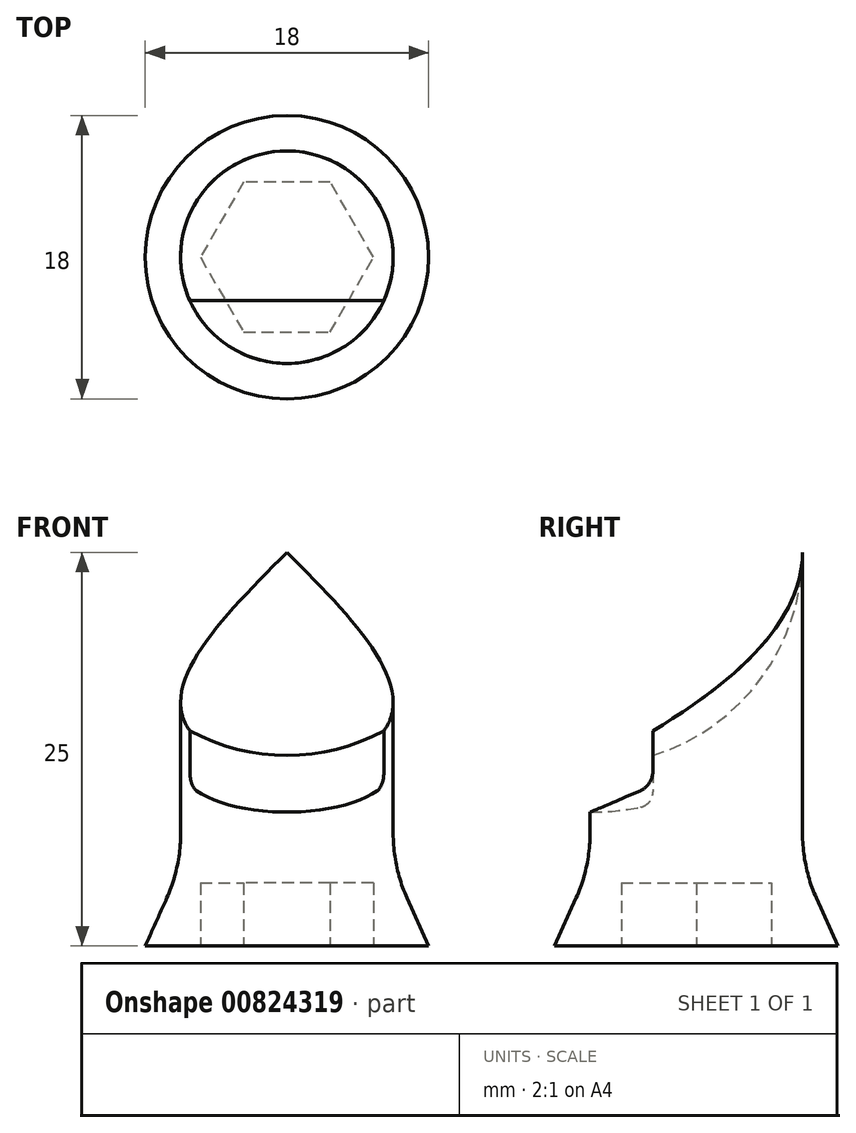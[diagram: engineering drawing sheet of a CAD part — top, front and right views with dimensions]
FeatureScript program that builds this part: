
annotation { "Feature Type Name" : "Feature", "Feature Type Description" : "" }
export const myFeature = defineFeature(function(context is Context, id is Id, definition is map)
    precondition{}
    {
        {
            var Q0;
            Q0=qCreatedBy(makeId("Right.planeOp"),FACE);
            var sketch = newSketch(context, id + "F0", { "sketchPlane" : qUnion([Q0])});
            skArc(sketch, "E0", {"start": v(11.5, 0) * mm, "mid": v(8.13, 8.13) * mm, "end": v(0, 11.5) * mm});
            skArc(sketch, "E1.0", {"start": v(13.5, 0) * mm, "mid": v(9.55, 9.55) * mm, "end": v(0, 13.5) * mm});
            skLineSegment(sketch, "E2", {"start": v(0, 13.5) * mm, "end": v(0, 11.5) * mm});
            skLineSegment(sketch, "E3.0", {"start": v(3, 15.75) * mm, "end": v(3, 13.75) * mm});
            skLineSegment(sketch, "E4.0", {"start": v(4, 15.2) * mm, "end": v(4, 12.9) * mm});
            skArc(sketch, "E5.0", {"start": v(3.2, 16.19) * mm, "mid": v(1.6, 16.42) * mm, "end": v(0, 16.5) * mm});
            skLineSegment(sketch, "E6", {"start": v(0, 16.5) * mm, "end": v(0, 16) * mm});
            skLineSegment(sketch, "E7.trimOffspring", {"start": v(2.75, 16) * mm, "end": v(0, 16) * mm});
            skArc(sketch, "E8.filletArc", {"start": v(4, 15.2) * mm, "mid": v(3.77, 15.84) * mm, "end": v(3.2, 16.19) * mm});
            skPoint(sketch, "E9.visualSharp", {"position": v(3, 16) * mm});
            skArc(sketch, "E9.filletArc", {"start": v(3, 15.75) * mm, "mid": v(2.93, 15.93) * mm, "end": v(2.75, 16) * mm});
            skLineSegment(sketch, "E10.0", {"start": v(2.75, 13.5) * mm, "end": v(0, 13.5) * mm});
            skPoint(sketch, "E11.visualSharp", {"position": v(3, 13.5) * mm});
            skArc(sketch, "E11.filletArc", {"start": v(2.75, 13.5) * mm, "mid": v(2.93, 13.57) * mm, "end": v(3, 13.75) * mm});
            skLineSegment(sketch, "E12", {"start": v(11.5, 0) * mm, "end": v(13.5, 0) * mm});
            skLineSegment(sketch, "E13", {"start": v(0, 0) * mm, "end": v(-5, 0) * mm, "construction": true});
            skPoint(sketch, "E14.orphan", {"position": v(13.5, 0) * mm});
            skLineSegment(sketch, "E15.bottom", {"start": v(6.75, 0) * mm, "end": v(13.5, 0) * mm});
            skLineSegment(sketch, "E15.right", {"start": v(13.5, 0) * mm, "end": v(13.5, -17.85) * mm});
            skLineSegment(sketch, "E16.0", {"start": v(6.75, -25) * mm, "end": v(15.75, -25) * mm});
            skLineSegment(sketch, "E17", {"start": v(6.75, -25) * mm, "end": v(6.75, 0) * mm});
            skLineSegment(sketch, "E18", {"start": v(14.38, -21.96) * mm, "end": v(15.75, -25) * mm});
            skPoint(sketch, "E19.visualSharp", {"position": v(0, -21.07) * mm});
            skPoint(sketch, "E20.visualSharp", {"position": v(13.5, -20) * mm});
            skArc(sketch, "E20.filletArc", {"start": v(13.5, -17.85) * mm, "mid": v(13.72, -19.95) * mm, "end": v(14.38, -21.96) * mm});
            skLineSegment(sketch, "E21", {"start": v(0, 11.5) * mm, "end": v(0, 0) * mm});
            skLineSegment(sketch, "E22", {"start": v(11.5, 0) * mm, "end": v(0, 0) * mm});
            skLineSegment(sketch, "E23", {"start": v(0, 13.5) * mm, "end": v(0, 16) * mm});
            skSolve(sketch);
        }
        {
            var Q0;
            Q0=makeQuery(id+"F0.imprint","IMPRINT",FACE,{"disambiguationData":[TD([[makeQuery(id+"F0.imprint","IMPRINT",EDGE,{"derivedFrom":sQuery(id+"F0.wireOp",EDGE,"E3.0")}),1.0]])]});
            var Q1;
            Q1=makeQuery(id+"F0.imprint","IMPRINT",FACE,{"disambiguationData":[TD([[makeQuery(id+"F0.imprint","IMPRINT",EDGE,{"derivedFrom":sQuery(id+"F0.wireOp",EDGE,"E0")}),-1.0]])]});
            var Q2;
            Q2=sQuery(id+"F0.wireOp",EDGE,"E13");
            revolve(context, id + "F1", {"surfaceOperationType" : NewSurfaceOperationType.NEW, "entities" : qUnion([Q0, Q1]), "axis" : qUnion([Q2]), "revolveType" : RevolveType.FULL});
        }
        {
            var Q0;
            {var subQ0=sQuery(id+"F0.wireOp",EDGE,"E15.right");Q0=makeQuery(id+"F0.imprint","IMPRINT",FACE,{"disambiguationData":[TD([[makeQuery(id+"F0.imprint","IMPRINT",EDGE,{"derivedFrom":subQ0}),-1.0]])]});}
            var Q1;
            Q1=sQuery(id+"F0.wireOp",EDGE,"E17");
            revolve(context, id + "F2", {"surfaceOperationType" : NewSurfaceOperationType.NEW, "entities" : qUnion([Q0]), "axis" : qUnion([Q1]), "revolveType" : RevolveType.FULL});
        }
        {
            var Q0;
            {var subQ0=sQuery(id+"F0.wireOp",EDGE,"E0");Q0=makeQuery(id+"F0.imprint","IMPRINT",FACE,{"disambiguationData":[TD([[makeQuery(id+"F0.imprint","IMPRINT",EDGE,{"derivedFrom":subQ0}),1.0]])]});}
            var Q1;
            Q1=makeQuery(id+"F0.imprint","IMPRINT",FACE,{"disambiguationData":[TD([[makeQuery(id+"F0.imprint","IMPRINT",EDGE,{"derivedFrom":sQuery(id+"F0.wireOp",EDGE,"E0")}),-1.0]])]});
            var Q2;
            Q2=makeQuery(id+"F0.imprint","IMPRINT",FACE,{"disambiguationData":[TD([[makeQuery(id+"F0.imprint","IMPRINT",EDGE,{"derivedFrom":sQuery(id+"F0.wireOp",EDGE,"E3.0")}),-1.0]])]});
            var Q3;
            Q3=makeQuery(id+"F0.imprint","IMPRINT",FACE,{"disambiguationData":[TD([[makeQuery(id+"F0.imprint","IMPRINT",EDGE,{"derivedFrom":sQuery(id+"F0.wireOp",EDGE,"E3.0")}),1.0]])]});
            var Q4;
            Q4=sQuery(id+"F0.wireOp",EDGE,"E13");
            revolve(context, id + "F3", {"operationType" : NewBodyOperationType.REMOVE, "surfaceOperationType" : NewSurfaceOperationType.NEW, "entities" : qUnion([Q0, Q1, Q2, Q3]), "axis" : qUnion([Q4]), "revolveType" : RevolveType.FULL, "oppositeDirection" : true});
        }
        {
            var Q0;
            Q0=makeQuery(id+"F2.opRevolve","SWEPT_FACE",FACE,{"disambiguationData":[OSD([sQuery(id+"F0.wireOp",EDGE,"E16.0")])]});
            var sketch = newSketch(context, id + "F4", { "sketchPlane" : qUnion([Q0])});
            skCircle(sketch, "E24.cCircle", {"center": v(0, -6.75) * mm, "radius": 5.5 * mm, "construction": true});
            skLineSegment(sketch, "E24.0", {"start": v(2.75, -11.51) * mm, "end": v(-2.75, -11.51) * mm});
            skLineSegment(sketch, "E24.1", {"start": v(-2.75, -11.51) * mm, "end": v(-5.5, -6.75) * mm});
            skLineSegment(sketch, "E24.2", {"start": v(-5.5, -6.75) * mm, "end": v(-2.75, -1.99) * mm});
            skLineSegment(sketch, "E24.3", {"start": v(-2.75, -1.99) * mm, "end": v(2.75, -1.99) * mm});
            skLineSegment(sketch, "E24.4", {"start": v(2.75, -1.99) * mm, "end": v(5.5, -6.75) * mm});
            skLineSegment(sketch, "E24.5", {"start": v(5.5, -6.75) * mm, "end": v(2.75, -11.51) * mm});
            skSolve(sketch);
        }
        {
            var Q0;
            Q0=makeQuery(id+"F4.imprint","IMPRINT",FACE,{"disambiguationData":[TD([[makeQuery(id+"F4.imprint","IMPRINT",EDGE,{"derivedFrom":sQuery(id+"F4.wireOp",EDGE,"E24.0")}),-1.0]])]});
            extrude(context, id + "F5", {"entities" : qUnion([Q0]), "operationType" : NewBodyOperationType.REMOVE, "oppositeDirection" : true, "depth" : 4 * mm, "offsetDistance" : 25 * mm});
        }
    });
